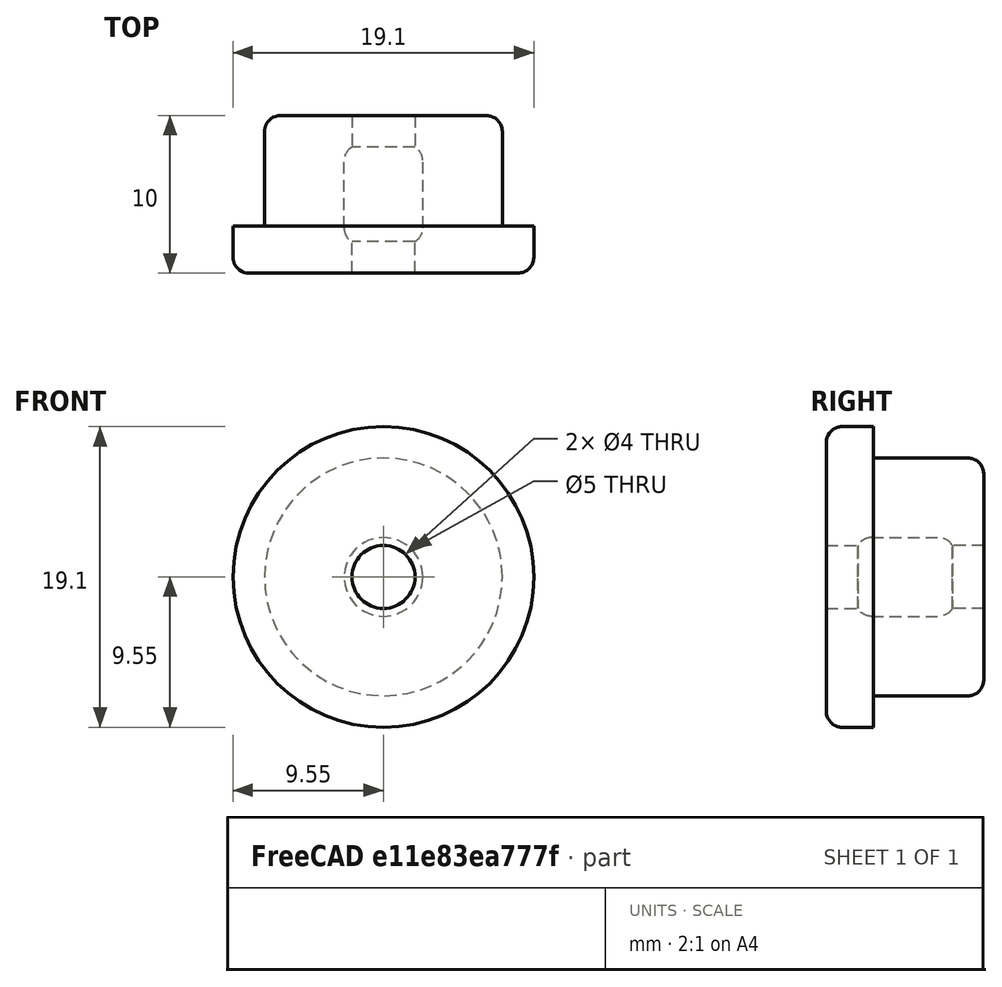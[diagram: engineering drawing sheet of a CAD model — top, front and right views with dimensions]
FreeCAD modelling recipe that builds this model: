
FCSTD DOCUMENT  (FreeCAD 0.20R29410 (Git))
Label: CD_adapter
License: All rights reserved
LicenseURL: http://en.wikipedia.org/wiki/All_rights_reserved
objects: PartDesign::Fillet×2, Spreadsheet::Sheet×1, Sketcher::SketchObject×1, PartDesign::Revolution×1, PartDesign::Body×1, App::Part×1, Mesh::Feature×1
note: 8 computed .brp shape members not serialized (recipe doc carries the construction recipe); baked Part::Feature solids carry a one-line shape summary decoded from their .brp

FEATURE [Spreadsheet::Sheet] Spreadsheet
  cells = A4=large_dia; B4(large_dia)=15.1; A6=Bamboo stick diameter; B6=3.5; A7=clearance; B7=0.5; A8=small_dia; B8(small_dia)==B6 + B7; A10=thickness; B10(thickness)=10
FEATURE [Sketcher::SketchObject] Sketch
  FullyConstrained = true
  MapMode = 5
  Support = -> [XY_Plane001]
  expr: Constraints[10] = Spreadsheet.small_dia / 2
  expr: Constraints[11] = Spreadsheet.large_dia / 2
  expr: Constraints[12] = Spreadsheet.small_dia / 2
  expr: Constraints[13] = Spreadsheet.thickness
  expr: Constraints[26] = Spreadsheet.small_dia / 2
  sketch-geometry (10):
    g0: LineSegment StartX=9.55 StartY=0 StartZ=0 EndX=9.55 EndY=3 EndZ=0
    g1: LineSegment StartX=9.55 StartY=3 StartZ=0 EndX=7.55 EndY=3 EndZ=0
    g2: LineSegment StartX=7.55 StartY=3 StartZ=0 EndX=7.55 EndY=10 EndZ=0
    g3: LineSegment StartX=7.55 StartY=10 StartZ=0 EndX=2 EndY=10 EndZ=0
    g4: LineSegment StartX=2 StartY=0 StartZ=0 EndX=9.55 EndY=0 EndZ=0
    g5: LineSegment StartX=2 StartY=10 StartZ=0 EndX=2 EndY=8 EndZ=0
    g6: LineSegment StartX=2 StartY=0 StartZ=0 EndX=2 EndY=2 EndZ=0
    g7: ArcOfCircle CenterX=1.5 CenterY=7.13397 CenterZ=0 NormalX=0 NormalY=0 NormalZ=1 AngleXU=0 Radius=1 StartAngle=3e-16 EndAngle=1.0472
    g8: ArcOfCircle CenterX=1.5 CenterY=2.86603 CenterZ=0 NormalX=0 NormalY=0 NormalZ=1 AngleXU=0 Radius=1 StartAngle=5.23599 EndAngle=6.28319
    g9: LineSegment StartX=2.5 StartY=2.86603 StartZ=0 EndX=2.5 EndY=7.13397 EndZ=0
  constraints (30):
    c: PointOnObject(g0,g-1)
    c: Vertical(g0)
    c: Coincident(g1,g0)
    c: Horizontal(g1)
    c: Coincident(g2,g1)
    c: Vertical(g2)
    c: Coincident(g3,g2)
    c: Horizontal(g3)
    c: Coincident(g4,g0)
    c: Horizontal(g4)
    c: Distance(g-1,g4) = 2
    c: DistanceX(g-1,g2) = 7.55
    c: DistanceX(g1,g0) = 2
    c: DistanceY(g4,g3) = 10
    c: DistanceY(g0,g0) = 3
    c: Coincident(g5,g3)
    c: Vertical(g5)
    c: Coincident(g6,g4)
    c: Vertical(g6)
    c: Equal(g6,g5)
    c: DistanceY(g5,g5) = 2
    c: Coincident(g7,g5)
    c: Coincident(g8,g6)
    c: Vertical(g9)
    c: Equal(g7,g8)
    c: Radius(g7) = 1
    c: DistanceX(g-1,g3) = 2
    c: Tangent(g9,g7) = -1.5708
    c: Tangent(g9,g8) = -1.5708
    c: DistanceX(g5,g7) = 0.5
FEATURE [PartDesign::Revolution] Revolution
  Angle = 360
  Axis = (0,1,0)
  Base = (0,0,0)
  Profile = -> Sketch
  ReferenceAxis = -> Sketch [V_Axis]
  Reversed = true
FEATURE [PartDesign::Fillet] Fillet
  Base = -> Revolution [Edge5]
  BaseFeature = -> Revolution
  Radius = 1
  SupportTransform = false
  UseAllEdges = false
FEATURE [PartDesign::Fillet] Fillet001
  Base = -> Fillet [Edge8]
  BaseFeature = -> Fillet
  Radius = 1
  SupportTransform = false
  UseAllEdges = false
FEATURE [PartDesign::Body] Body
  Group = -> [Sketch,Revolution,Fillet,Fillet001]
  Origin = -> Origin001
  Tip = -> Fillet001
FEATURE [App::Part] Part
  Group = -> [Body]
  Origin = -> Origin
FEATURE [Mesh::Feature] Mesh  label="Body (Meshed)"
